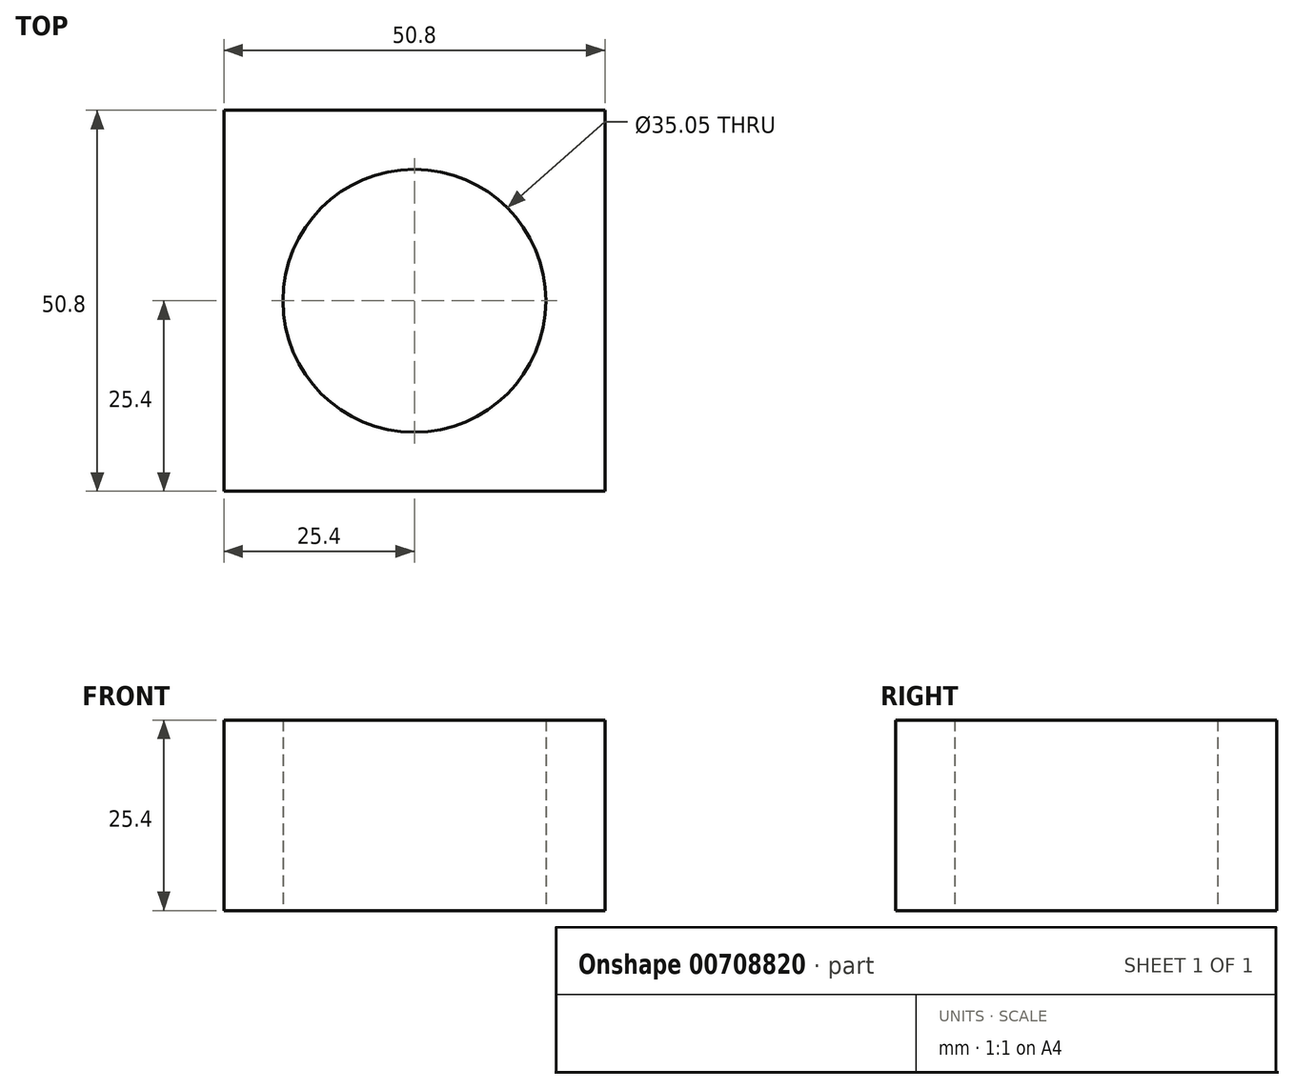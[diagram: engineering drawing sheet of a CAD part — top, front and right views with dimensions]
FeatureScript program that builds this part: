
annotation { "Feature Type Name" : "Feature", "Feature Type Description" : "" }
export const myFeature = defineFeature(function(context is Context, id is Id, definition is map)
    precondition{}
    {
        {
            var Q0;
            Q0=qCreatedBy(makeId("Top.planeOp"),FACE);
            var sketch = newSketch(context, id + "F0", { "sketchPlane" : qUnion([Q0])});
            skLineSegment(sketch, "E0.bottom", {"start": v(0, 0) * mm, "end": v(50.8, 0) * mm});
            skLineSegment(sketch, "E0.top", {"start": v(0, 50.8) * mm, "end": v(50.8, 50.8) * mm});
            skLineSegment(sketch, "E0.left", {"start": v(0, 0) * mm, "end": v(0, 50.8) * mm});
            skLineSegment(sketch, "E0.right", {"start": v(50.8, 0) * mm, "end": v(50.8, 50.8) * mm});
            skCircle(sketch, "E1", {"center": v(25.4, 25.4) * mm, "radius": 17.53 * mm});
            skLineSegment(sketch, "E2", {"start": v(25.4, 50.8) * mm, "end": v(25.4, 0) * mm, "construction": true});
            skSolve(sketch);
        }
        {
            var Q0;
            Q0 = qSketchRegion(id + "F0", true);
            extrude(context, id + "F1", {"entities" : qUnion([Q0]), "depth" : 25.4 * mm, "offsetDistance" : 25.4 * mm});
        }
    });
